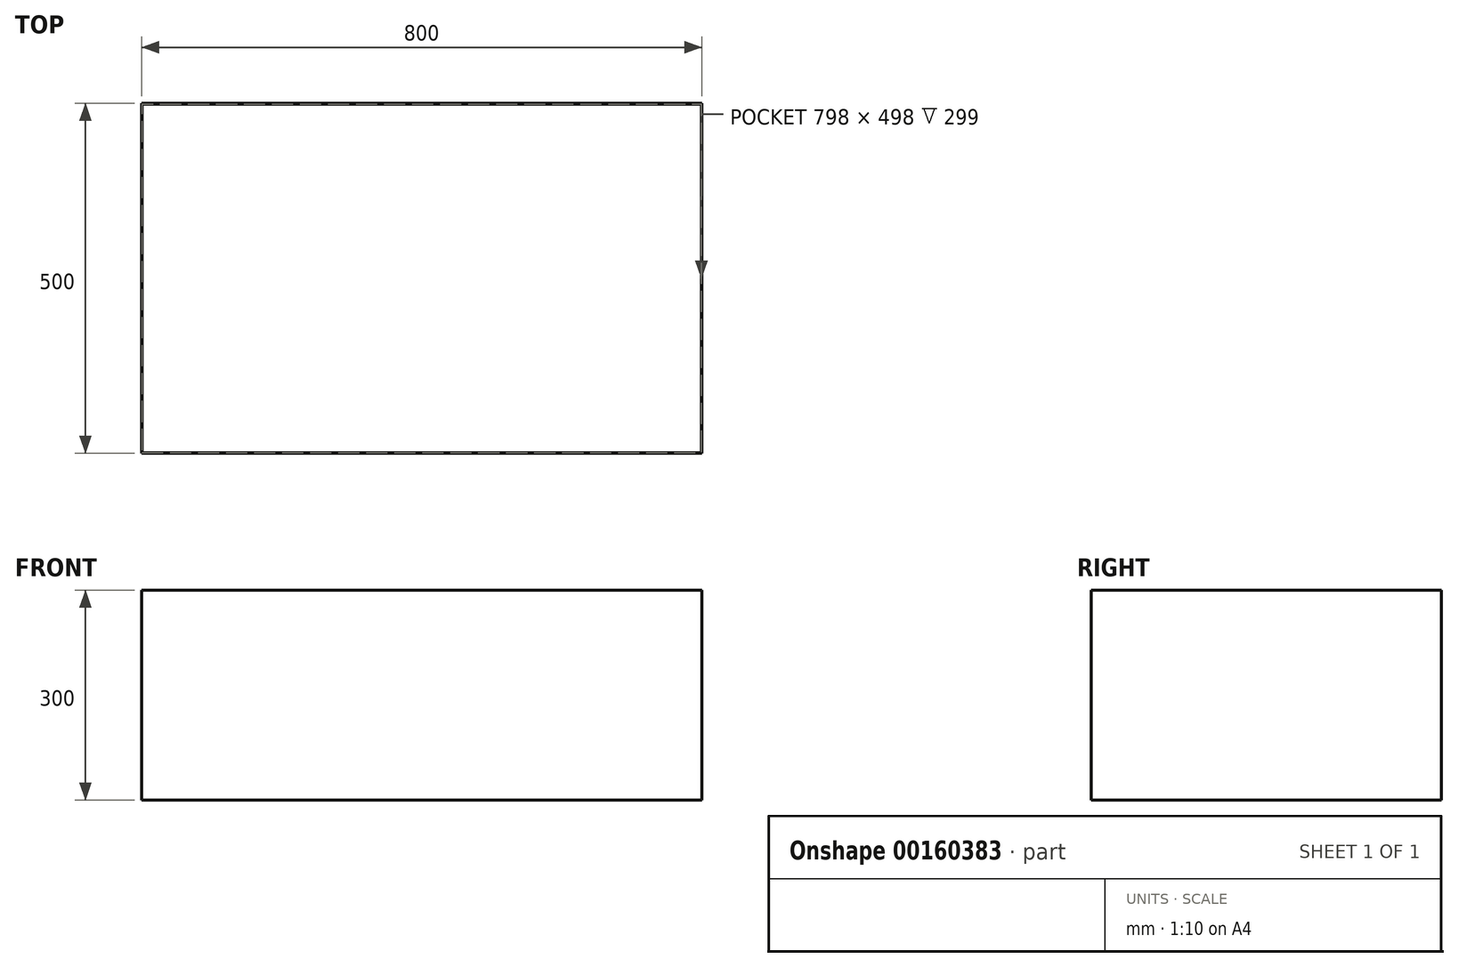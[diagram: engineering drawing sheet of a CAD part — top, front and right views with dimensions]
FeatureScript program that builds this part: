
annotation { "Feature Type Name" : "Feature", "Feature Type Description" : "" }
export const myFeature = defineFeature(function(context is Context, id is Id, definition is map)
    precondition{}
    {
        {
            var Q0;
            Q0=qCreatedBy(makeId("Top.planeOp"),FACE);
            var sketch = newSketch(context, id + "F0", { "sketchPlane" : qUnion([Q0])});
            skLineSegment(sketch, "E0.bottom", {"start": v(0, 0) * mm, "end": v(800, 0) * mm});
            skLineSegment(sketch, "E0.top", {"start": v(0, 500) * mm, "end": v(800, 500) * mm});
            skLineSegment(sketch, "E0.left", {"start": v(0, 0) * mm, "end": v(0, 500) * mm});
            skLineSegment(sketch, "E0.right", {"start": v(800, 0) * mm, "end": v(800, 500) * mm});
            skSolve(sketch);
        }
        {
            var Q0;
            Q0 = qSketchRegion(id + "F0", true);
            extrude(context, id + "F1", {"entities" : qUnion([Q0]), "depth" : 300 * mm});
        }
        {
            var Q0;
            Q0=makeQuery(id+"F1.opExtrude","CAP_FACE",FACE,{"disambiguationData":[OSD([sQuery(id+"F0.wireOp",EDGE,"E0.bottom"),sQuery(id+"F0.wireOp",EDGE,"E0.top"),sQuery(id+"F0.wireOp",EDGE,"E0.left"),sQuery(id+"F0.wireOp",EDGE,"E0.right")])],"isStart":false});
            shell(context, id + "F2", {"entities" : qUnion([Q0]), "thickness" : 1 * mm});
        }
        {
            var Q0;
            Q0=qCreatedBy(makeId("Right.planeOp"),FACE);
            var sketch = newSketch(context, id + "F3", { "sketchPlane" : qUnion([Q0])});
            skLineSegment(sketch, "E1", {"start": v(0, 0) * mm, "end": v(-25, 0) * mm});
            skLineSegment(sketch, "E2", {"start": v(-25, 0) * mm, "end": v(-25, 25) * mm});
            skLineSegment(sketch, "E3", {"start": v(-25, 25) * mm, "end": v(-23, 25) * mm});
            skLineSegment(sketch, "E4", {"start": v(-23, 25) * mm, "end": v(-23, 2) * mm});
            skLineSegment(sketch, "E5", {"start": v(-23, 2) * mm, "end": v(0, 2) * mm});
            skLineSegment(sketch, "E6", {"start": v(0, 2) * mm, "end": v(0, 0) * mm});
            skSolve(sketch);
        }
        {
            var Q0;
            Q0 = qSketchRegion(id + "F3", true);
            extrude(context, id + "F4", {"entities" : qUnion([Q0]), "depth" : 798 * mm});
        }
        {
            var Q0;
            Q0=makeQuery(id+"F4.opExtrude","SWEPT_BODY",BODY,{"disambiguationData":[OSD([sQuery(id+"F3.wireOp",EDGE,"E1"),sQuery(id+"F3.wireOp",EDGE,"E2"),sQuery(id+"F3.wireOp",EDGE,"E3"),sQuery(id+"F3.wireOp",EDGE,"E4"),sQuery(id+"F3.wireOp",EDGE,"E5"),sQuery(id+"F3.wireOp",EDGE,"E6")])]});
            deleteBodies(context, id + "F5", {"entities" : qUnion([Q0])});
        }
    });
